# Revit family: MT-HB_BIFOLD DOOR_XXXXXX
name_source: partatom
category: Doors
revit_build: Autodesk Revit 2017 (Build: 20160225_1515(x64)
units: mm (PartAtom-declared; Revit-internal decimal feet)

## family parameters
Always vertical = Yes
Cut with Voids When Loaded = No
Host = Wall
OmniClass Number = 23.30.20.00
OmniClass Title = Windows
Room Calculation Point = No
Shared = No

## types (3) — shared parameters
A = 4 mm  [stored 0.0131234 ft]
ANZRC COMPLIANT = YES
Analytic Construction = <None>
DOUBLE GLAZED THICKNESS = 18 mm  [stored 0.0590551 ft]
FRAME MATERIAL = <By Category>
GLAZED MATERIAL = Glass
MAX HEIGHT = 3000 mm  [stored 9.84252 ft]
MAX PANEL HEIGHT = 3000 mm  [stored 9.84252 ft]
MAX PANEL WIDTH = 1000 mm  [stored 3.28084 ft]
MAX WIDTH = 6000 mm  [stored 19.685 ft]
Manufacturer = ALSPEC
Model = HAWKESBURY TOP HUNG COMMERCIAL MULTI-FOLD DOOR
OFFSET = 10 mm  [stored 0.0328084 ft]
SINGLE GLAZED THICKNESS = 5 mm  [stored 0.0164042 ft]
URL = WWW.ALSPEC.COM.AU
VERSION = 2.1
WARNING = No
Wall Closure = By host
YEAR = 2019
zero-valued in all types: Default Sill Height

## per-type parameters (varying)
| type | 101.6mm FRAME THICKNESS | 150mm FRAME THICKNESS | AIR POCKET | BOT PANEL POSITION | DETAIL_DEPTH SILL | DOUBLE GLAZED | FRAME THICKNESS | Height | OVERALL FRAME HEIGHT | OVERALL FRAME WIDTH | PANEL HEIGHT | PANEL WIDTH | Rough Height | Rough Width | TOLERANCE | TOP PANEL POSITION | Width |
| 4L1R/1L4R | No | Yes | 8 mm  [stored 0.0262467 ft] | 95 mm | 150 mm | No | 76 mm  [stored 0.249344 ft] | 2100 mm | 2100 mm | 3500 mm  [stored 11.4829 ft] | 1907 mm | 563 mm | 2200 mm | 3600 mm  [stored 11.811 ft] | 50 mm  [stored 0.164042 ft] | 1891 mm | 3500 mm  [stored 11.4829 ft] |
| 3L3R | Yes | No | 5 mm  [stored 0.0164042 ft] | 35 mm | 102 mm | Yes | 102 mm | 2700 mm  [stored 8.85827 ft] | 2700 mm  [stored 8.85827 ft] | 4500 mm | 2582 mm | 730 mm | 2700 mm  [stored 8.85827 ft] | 4500 mm | 0 mm  [stored 0 ft] | 2566 mm | 4500 mm |
| 5L/5R | No | Yes | 8 mm  [stored 0.0262467 ft] | 95 mm | 150 mm | No | 76 mm  [stored 0.249344 ft] | 2100 mm | 2100 mm | 3500 mm  [stored 11.4829 ft] | 1907 mm | 563 mm | 2200 mm | 3600 mm  [stored 11.811 ft] | 50 mm  [stored 0.164042 ft] | 1891 mm | 3500 mm  [stored 11.4829 ft] |

note: [stored X ft] marks values corroborated as IEEE doubles in the binary element streams (Revit-internal decimal feet)

## geometry (parser evidence)
native form markers: Extrusion x2, Sweep x34
no freeform markers — native parametric forms only
